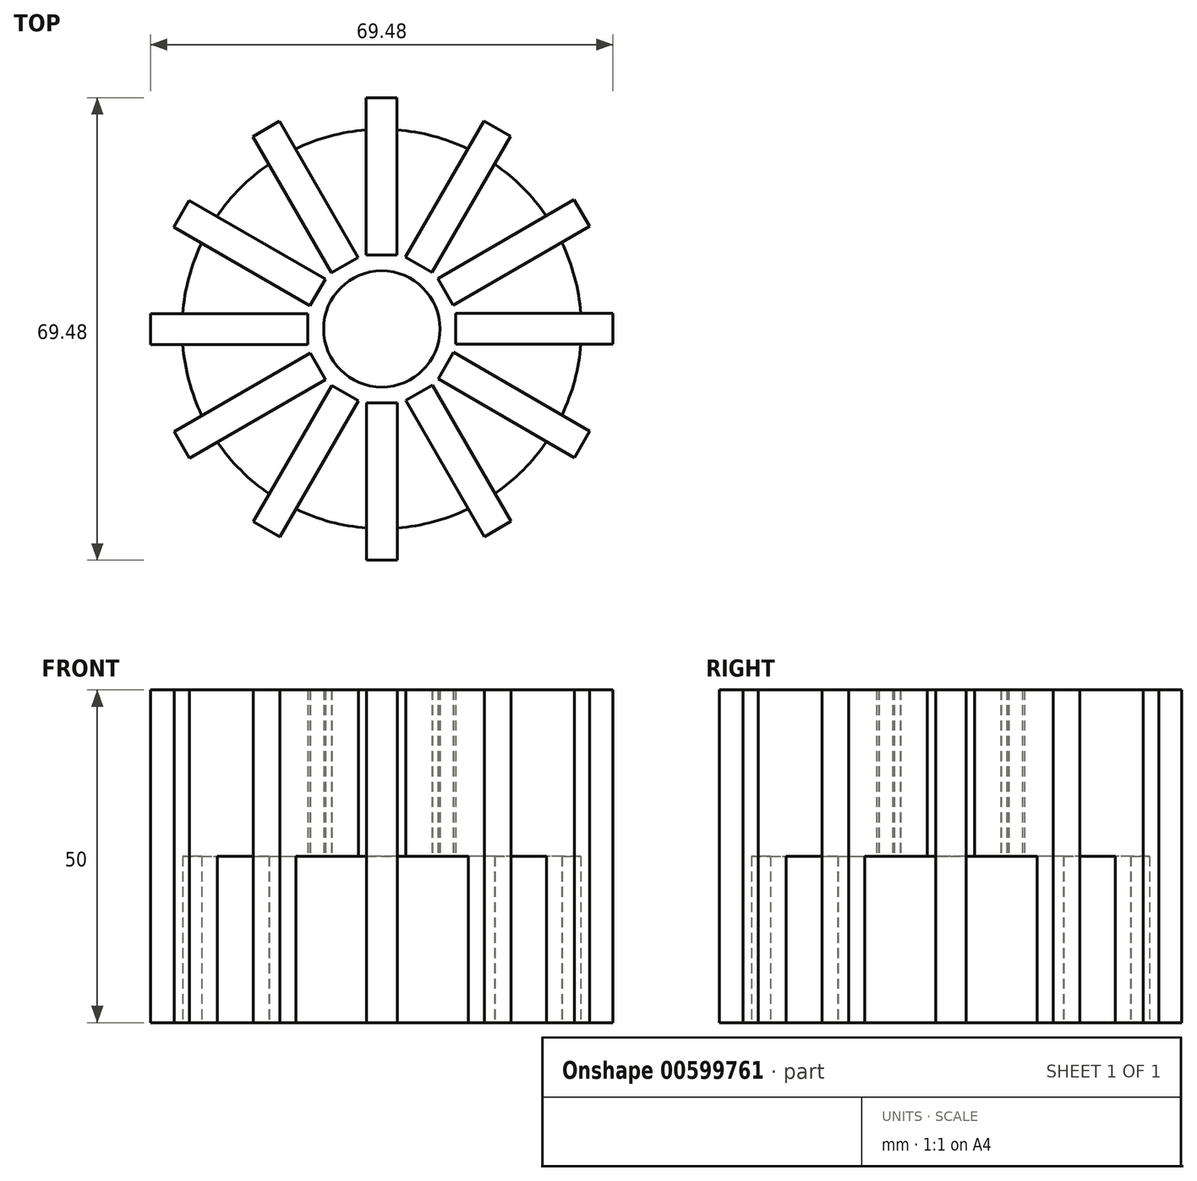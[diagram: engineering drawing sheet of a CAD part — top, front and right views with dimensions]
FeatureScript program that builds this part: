
annotation { "Feature Type Name" : "Feature", "Feature Type Description" : "" }
export const myFeature = defineFeature(function(context is Context, id is Id, definition is map)
    precondition{}
    {
        {
            var Q0;
            Q0=qCreatedBy(makeId("Top.planeOp"),FACE);
            var sketch = newSketch(context, id + "F0", { "sketchPlane" : qUnion([Q0])});
            skCircle(sketch, "E0", {"center": v(0, 0) * mm, "radius": 30 * mm});
            skLineSegment(sketch, "E1.bottom", {"start": v(-2.35, 34.74) * mm, "end": v(2.27, 34.74) * mm});
            skLineSegment(sketch, "E1.top", {"start": v(-2.35, 11.1) * mm, "end": v(2.27, 11.1) * mm});
            skLineSegment(sketch, "E1.left", {"start": v(-2.35, 34.74) * mm, "end": v(-2.35, 11.1) * mm});
            skLineSegment(sketch, "E1.right", {"start": v(2.27, 34.74) * mm, "end": v(2.27, 11.1) * mm});
            skLineSegment(sketch, "E2.1.0", {"start": v(-19.4, 28.91) * mm, "end": v(-7.59, 8.45) * mm});
            skLineSegment(sketch, "E2.1.1", {"start": v(-7.59, 8.45) * mm, "end": v(-3.59, 10.75) * mm});
            skLineSegment(sketch, "E2.1.2", {"start": v(-15.4, 31.22) * mm, "end": v(-3.59, 10.75) * mm});
            skLineSegment(sketch, "E2.1.3", {"start": v(-19.4, 28.91) * mm, "end": v(-15.4, 31.22) * mm});
            skLineSegment(sketch, "E2.2.0", {"start": v(-31.26, 15.34) * mm, "end": v(-10.8, 3.52) * mm});
            skLineSegment(sketch, "E2.2.1", {"start": v(-10.8, 3.52) * mm, "end": v(-8.48, 7.52) * mm});
            skLineSegment(sketch, "E2.2.2", {"start": v(-28.95, 19.34) * mm, "end": v(-8.48, 7.52) * mm});
            skLineSegment(sketch, "E2.2.3", {"start": v(-31.26, 15.34) * mm, "end": v(-28.95, 19.34) * mm});
            skLineSegment(sketch, "E2.3.0", {"start": v(-34.74, -2.35) * mm, "end": v(-11.1, -2.35) * mm});
            skLineSegment(sketch, "E2.3.1", {"start": v(-11.1, -2.35) * mm, "end": v(-11.1, 2.27) * mm});
            skLineSegment(sketch, "E2.3.2", {"start": v(-34.74, 2.27) * mm, "end": v(-11.1, 2.27) * mm});
            skLineSegment(sketch, "E2.3.3", {"start": v(-34.74, -2.35) * mm, "end": v(-34.74, 2.27) * mm});
            skLineSegment(sketch, "E2.4.0", {"start": v(-28.91, -19.4) * mm, "end": v(-8.45, -7.59) * mm});
            skLineSegment(sketch, "E2.4.1", {"start": v(-8.45, -7.59) * mm, "end": v(-10.75, -3.59) * mm});
            skLineSegment(sketch, "E2.4.2", {"start": v(-31.22, -15.4) * mm, "end": v(-10.75, -3.59) * mm});
            skLineSegment(sketch, "E2.4.3", {"start": v(-28.91, -19.4) * mm, "end": v(-31.22, -15.4) * mm});
            skLineSegment(sketch, "E2.5.0", {"start": v(-15.34, -31.26) * mm, "end": v(-3.52, -10.8) * mm});
            skLineSegment(sketch, "E2.5.1", {"start": v(-3.52, -10.8) * mm, "end": v(-7.52, -8.48) * mm});
            skLineSegment(sketch, "E2.5.2", {"start": v(-19.34, -28.95) * mm, "end": v(-7.52, -8.48) * mm});
            skLineSegment(sketch, "E2.5.3", {"start": v(-15.34, -31.26) * mm, "end": v(-19.34, -28.95) * mm});
            skLineSegment(sketch, "E2.6.0", {"start": v(2.35, -34.74) * mm, "end": v(2.35, -11.1) * mm});
            skLineSegment(sketch, "E2.6.1", {"start": v(2.35, -11.1) * mm, "end": v(-2.27, -11.1) * mm});
            skLineSegment(sketch, "E2.6.2", {"start": v(-2.27, -34.74) * mm, "end": v(-2.27, -11.1) * mm});
            skLineSegment(sketch, "E2.6.3", {"start": v(2.35, -34.74) * mm, "end": v(-2.27, -34.74) * mm});
            skLineSegment(sketch, "E2.7.0", {"start": v(19.4, -28.91) * mm, "end": v(7.59, -8.45) * mm});
            skLineSegment(sketch, "E2.7.1", {"start": v(7.59, -8.45) * mm, "end": v(3.59, -10.75) * mm});
            skLineSegment(sketch, "E2.7.2", {"start": v(15.4, -31.22) * mm, "end": v(3.59, -10.75) * mm});
            skLineSegment(sketch, "E2.7.3", {"start": v(19.4, -28.91) * mm, "end": v(15.4, -31.22) * mm});
            skLineSegment(sketch, "E2.8.0", {"start": v(31.26, -15.34) * mm, "end": v(10.8, -3.52) * mm});
            skLineSegment(sketch, "E2.8.1", {"start": v(10.8, -3.52) * mm, "end": v(8.48, -7.52) * mm});
            skLineSegment(sketch, "E2.8.2", {"start": v(28.95, -19.34) * mm, "end": v(8.48, -7.52) * mm});
            skLineSegment(sketch, "E2.8.3", {"start": v(31.26, -15.34) * mm, "end": v(28.95, -19.34) * mm});
            skLineSegment(sketch, "E2.9.0", {"start": v(34.74, 2.35) * mm, "end": v(11.1, 2.35) * mm});
            skLineSegment(sketch, "E2.9.1", {"start": v(11.1, 2.35) * mm, "end": v(11.1, -2.27) * mm});
            skLineSegment(sketch, "E2.9.2", {"start": v(34.74, -2.27) * mm, "end": v(11.1, -2.27) * mm});
            skLineSegment(sketch, "E2.9.3", {"start": v(34.74, 2.35) * mm, "end": v(34.74, -2.27) * mm});
            skLineSegment(sketch, "E2.10.0", {"start": v(28.91, 19.4) * mm, "end": v(8.45, 7.59) * mm});
            skLineSegment(sketch, "E2.10.1", {"start": v(8.45, 7.59) * mm, "end": v(10.75, 3.59) * mm});
            skLineSegment(sketch, "E2.10.2", {"start": v(31.22, 15.4) * mm, "end": v(10.75, 3.59) * mm});
            skLineSegment(sketch, "E2.10.3", {"start": v(28.91, 19.4) * mm, "end": v(31.22, 15.4) * mm});
            skLineSegment(sketch, "E2.11.0", {"start": v(15.34, 31.26) * mm, "end": v(3.52, 10.8) * mm});
            skLineSegment(sketch, "E2.11.1", {"start": v(3.52, 10.8) * mm, "end": v(7.52, 8.48) * mm});
            skLineSegment(sketch, "E2.11.2", {"start": v(19.34, 28.95) * mm, "end": v(7.52, 8.48) * mm});
            skLineSegment(sketch, "E2.11.3", {"start": v(15.34, 31.26) * mm, "end": v(19.34, 28.95) * mm});
            skCircle(sketch, "E3", {"center": v(0, 0) * mm, "radius": 8.73 * mm});
            skSolve(sketch);
        }
        {
            var Q0;
            {var subQ50=sQuery(id+"F0.wireOp",EDGE,"E1.top");Q0=makeQuery(id+"F0.imprint","IMPRINT",FACE,{"disambiguationData":[TD([[makeQuery(id+"F0.imprint","IMPRINT",EDGE,{"derivedFrom":subQ50}),-1.0]])]});}
            extrude(context, id + "F1", {"entities" : qUnion([Q0]), "depth" : 25 * mm, "offsetDistance" : 25 * mm});
        }
        {
            var Q0;
            {var subQ5=sQuery(id+"F0.wireOp",EDGE,"E2.2.3");Q0=makeQuery(id+"F0.imprint","IMPRINT",FACE,{"disambiguationData":[TD([[makeQuery(id+"F0.imprint","IMPRINT",EDGE,{"derivedFrom":subQ5}),-1.0]])]});}
            var Q1;
            {var subQ5=sQuery(id+"F0.wireOp",EDGE,"E2.1.3");Q1=makeQuery(id+"F0.imprint","IMPRINT",FACE,{"disambiguationData":[TD([[makeQuery(id+"F0.imprint","IMPRINT",EDGE,{"derivedFrom":subQ5}),-1.0]])]});}
            var Q2;
            {var subQ5=sQuery(id+"F0.wireOp",EDGE,"E1.bottom");Q2=makeQuery(id+"F0.imprint","IMPRINT",FACE,{"disambiguationData":[TD([[makeQuery(id+"F0.imprint","IMPRINT",EDGE,{"derivedFrom":subQ5}),-1.0]])]});}
            var Q3;
            {var subQ5=sQuery(id+"F0.wireOp",EDGE,"E2.11.3");Q3=makeQuery(id+"F0.imprint","IMPRINT",FACE,{"disambiguationData":[TD([[makeQuery(id+"F0.imprint","IMPRINT",EDGE,{"derivedFrom":subQ5}),-1.0]])]});}
            var Q4;
            {var subQ5=sQuery(id+"F0.wireOp",EDGE,"E2.10.3");Q4=makeQuery(id+"F0.imprint","IMPRINT",FACE,{"disambiguationData":[TD([[makeQuery(id+"F0.imprint","IMPRINT",EDGE,{"derivedFrom":subQ5}),-1.0]])]});}
            var Q5;
            {var subQ5=sQuery(id+"F0.wireOp",EDGE,"E2.9.3");Q5=makeQuery(id+"F0.imprint","IMPRINT",FACE,{"disambiguationData":[TD([[makeQuery(id+"F0.imprint","IMPRINT",EDGE,{"derivedFrom":subQ5}),-1.0]])]});}
            var Q6;
            {var subQ5=sQuery(id+"F0.wireOp",EDGE,"E2.8.3");Q6=makeQuery(id+"F0.imprint","IMPRINT",FACE,{"disambiguationData":[TD([[makeQuery(id+"F0.imprint","IMPRINT",EDGE,{"derivedFrom":subQ5}),-1.0]])]});}
            var Q7;
            {var subQ5=sQuery(id+"F0.wireOp",EDGE,"E2.7.3");Q7=makeQuery(id+"F0.imprint","IMPRINT",FACE,{"disambiguationData":[TD([[makeQuery(id+"F0.imprint","IMPRINT",EDGE,{"derivedFrom":subQ5}),-1.0]])]});}
            var Q8;
            {var subQ5=sQuery(id+"F0.wireOp",EDGE,"E2.7.1");Q8=makeQuery(id+"F0.imprint","IMPRINT",FACE,{"disambiguationData":[TD([[makeQuery(id+"F0.imprint","IMPRINT",EDGE,{"derivedFrom":subQ5}),1.0]])]});}
            var Q9;
            {var subQ5=sQuery(id+"F0.wireOp",EDGE,"E2.8.1");Q9=makeQuery(id+"F0.imprint","IMPRINT",FACE,{"disambiguationData":[TD([[makeQuery(id+"F0.imprint","IMPRINT",EDGE,{"derivedFrom":subQ5}),1.0]])]});}
            var Q10;
            {var subQ5=sQuery(id+"F0.wireOp",EDGE,"E2.9.1");Q10=makeQuery(id+"F0.imprint","IMPRINT",FACE,{"disambiguationData":[TD([[makeQuery(id+"F0.imprint","IMPRINT",EDGE,{"derivedFrom":subQ5}),1.0]])]});}
            var Q11;
            {var subQ5=sQuery(id+"F0.wireOp",EDGE,"E2.10.1");Q11=makeQuery(id+"F0.imprint","IMPRINT",FACE,{"disambiguationData":[TD([[makeQuery(id+"F0.imprint","IMPRINT",EDGE,{"derivedFrom":subQ5}),1.0]])]});}
            var Q12;
            {var subQ5=sQuery(id+"F0.wireOp",EDGE,"E2.11.1");Q12=makeQuery(id+"F0.imprint","IMPRINT",FACE,{"disambiguationData":[TD([[makeQuery(id+"F0.imprint","IMPRINT",EDGE,{"derivedFrom":subQ5}),1.0]])]});}
            var Q13;
            {var subQ5=sQuery(id+"F0.wireOp",EDGE,"E1.top");Q13=makeQuery(id+"F0.imprint","IMPRINT",FACE,{"disambiguationData":[TD([[makeQuery(id+"F0.imprint","IMPRINT",EDGE,{"derivedFrom":subQ5}),1.0]])]});}
            var Q14;
            {var subQ5=sQuery(id+"F0.wireOp",EDGE,"E2.1.1");Q14=makeQuery(id+"F0.imprint","IMPRINT",FACE,{"disambiguationData":[TD([[makeQuery(id+"F0.imprint","IMPRINT",EDGE,{"derivedFrom":subQ5}),1.0]])]});}
            var Q15;
            {var subQ5=sQuery(id+"F0.wireOp",EDGE,"E2.2.1");Q15=makeQuery(id+"F0.imprint","IMPRINT",FACE,{"disambiguationData":[TD([[makeQuery(id+"F0.imprint","IMPRINT",EDGE,{"derivedFrom":subQ5}),1.0]])]});}
            var Q16;
            {var subQ5=sQuery(id+"F0.wireOp",EDGE,"E2.3.3");Q16=makeQuery(id+"F0.imprint","IMPRINT",FACE,{"disambiguationData":[TD([[makeQuery(id+"F0.imprint","IMPRINT",EDGE,{"derivedFrom":subQ5}),-1.0]])]});}
            var Q17;
            {var subQ5=sQuery(id+"F0.wireOp",EDGE,"E2.4.3");Q17=makeQuery(id+"F0.imprint","IMPRINT",FACE,{"disambiguationData":[TD([[makeQuery(id+"F0.imprint","IMPRINT",EDGE,{"derivedFrom":subQ5}),-1.0]])]});}
            var Q18;
            {var subQ5=sQuery(id+"F0.wireOp",EDGE,"E2.4.1");Q18=makeQuery(id+"F0.imprint","IMPRINT",FACE,{"disambiguationData":[TD([[makeQuery(id+"F0.imprint","IMPRINT",EDGE,{"derivedFrom":subQ5}),1.0]])]});}
            var Q19;
            {var subQ5=sQuery(id+"F0.wireOp",EDGE,"E2.5.1");Q19=makeQuery(id+"F0.imprint","IMPRINT",FACE,{"disambiguationData":[TD([[makeQuery(id+"F0.imprint","IMPRINT",EDGE,{"derivedFrom":subQ5}),1.0]])]});}
            var Q20;
            {var subQ5=sQuery(id+"F0.wireOp",EDGE,"E2.5.3");Q20=makeQuery(id+"F0.imprint","IMPRINT",FACE,{"disambiguationData":[TD([[makeQuery(id+"F0.imprint","IMPRINT",EDGE,{"derivedFrom":subQ5}),-1.0]])]});}
            var Q21;
            {var subQ5=sQuery(id+"F0.wireOp",EDGE,"E2.6.1");Q21=makeQuery(id+"F0.imprint","IMPRINT",FACE,{"disambiguationData":[TD([[makeQuery(id+"F0.imprint","IMPRINT",EDGE,{"derivedFrom":subQ5}),1.0]])]});}
            var Q22;
            {var subQ5=sQuery(id+"F0.wireOp",EDGE,"E2.6.3");Q22=makeQuery(id+"F0.imprint","IMPRINT",FACE,{"disambiguationData":[TD([[makeQuery(id+"F0.imprint","IMPRINT",EDGE,{"derivedFrom":subQ5}),-1.0]])]});}
            var Q23;
            Q23=makeQuery(id+"F0.imprint","IMPRINT",FACE,{"disambiguationData":[TD([[makeQuery(id+"F0.imprint","IMPRINT",EDGE,{"derivedFrom":sQuery(id+"F0.wireOp",EDGE,"E3")}),1.0]])]});
            var Q24;
            {var subQ5=sQuery(id+"F0.wireOp",EDGE,"E2.3.1");Q24=makeQuery(id+"F0.imprint","IMPRINT",FACE,{"disambiguationData":[TD([[makeQuery(id+"F0.imprint","IMPRINT",EDGE,{"derivedFrom":subQ5}),1.0]])]});}
            extrude(context, id + "F2", {"entities" : qUnion([Q0, Q1, Q2, Q3, Q4, Q5, Q6, Q7, Q8, Q9, Q10, Q11, Q12, Q13, Q14, Q15, Q16, Q17, Q18, Q19, Q20, Q21, Q22, Q23, Q24]), "operationType" : NewBodyOperationType.ADD, "depth" : 50 * mm, "offsetDistance" : 25 * mm});
        }
    });
